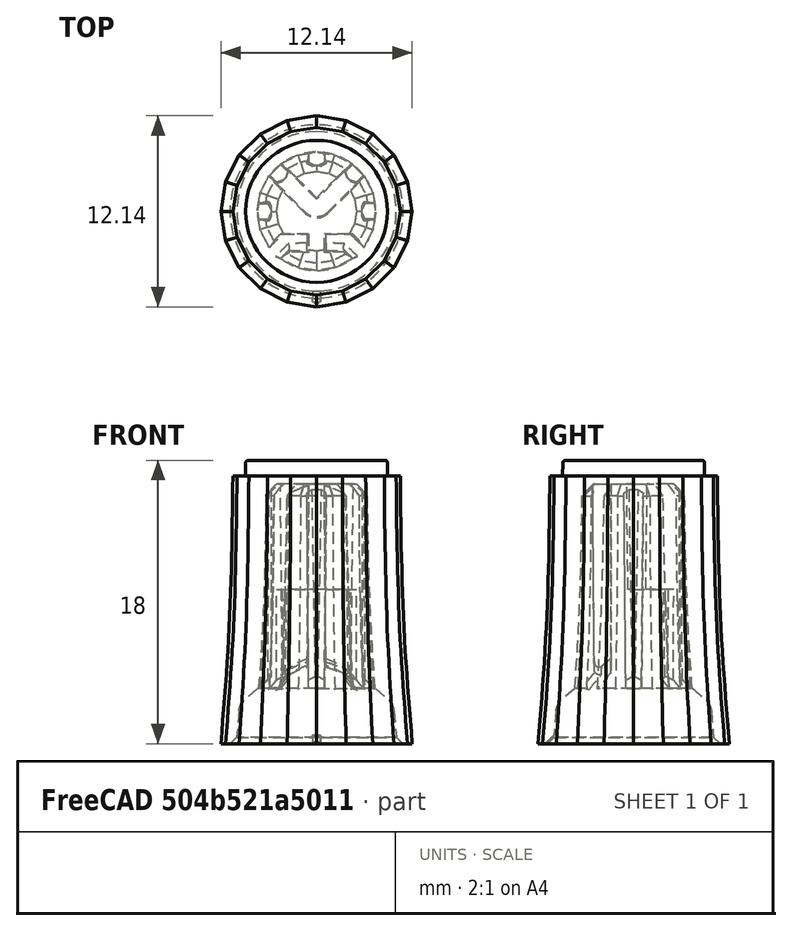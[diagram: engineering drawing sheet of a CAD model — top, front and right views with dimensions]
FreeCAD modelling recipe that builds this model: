
FCSTD DOCUMENT  (FreeCAD 0.21R33668 +26 (Git))
Label: PLASTIC-KNOB-ENC
License: All rights reserved
LicenseURL: https://en.wikipedia.org/wiki/All_rights_reserved
objects: TechDraw::DrawViewDimension×9, TechDraw::DrawHatch×8, TechDraw::DrawViewPart×5, Part::Feature×1, PartDesign::Boolean×1, TechDraw::DrawSVGTemplate×1, Sketcher::SketchObject×1, PartDesign::Body×1, TechDraw::DrawComplexSection×1, TechDraw::DrawViewBalloon×1, TechDraw::DrawPage×1
note: 21 computed .brp shape members not serialized (recipe doc carries the construction recipe); baked Part::Feature solids carry a one-line shape summary decoded from their .brp

FEATURE [Part::Feature] Part__Feature  label="potmeter"
  shape: bbox 15.71 x 15.32 x 34.99 mm, 134 faces (baked)
FEATURE [PartDesign::Boolean] Boolean
  Group = -> [Part__Feature]
  Type = 0
FEATURE [TechDraw::DrawSVGTemplate] Template
  EditableTexts = COLOR=Black - RAL code: 9004; CreationDate=2024/01/02; E.G.APPROVED=APPROVED; FC-Scale=5:1; FC-Title=PLASTIC - KNOB - ENC; IntechStudioLtd.=Intech Studio Ltd.; MATERIAL=ABS - Terluran GP22; REV=02; STANDARD=DIN 16742-TG4
  Height = 297
  Orientation = 1
  Template = <userpath>/Documents/grid-hardware/Manufacturing/FreeCAD_technical_drawing_template/A3_LandscapeTD_MODIFIED.svg
  Width = 420
FEATURE [Sketcher::SketchObject] Sketch
  FullyConstrained = true
  MapMode = 5
  Placement = pos=(0,0,0) rot=(1,0,0;1.5708rad)
  Support = -> [XZ_Plane]
  sketch-geometry (1):
    g0: LineSegment StartX=0 StartY=19 StartZ=0 EndX=0 EndY=-1 EndZ=0
  constraints (4):
    c: PointOnObject(g0,g-2)
    c: Vertical(g0)
    c: DistanceY(g0,g0) = 20
    c: DistanceY(g0,g-1) = 1
FEATURE [PartDesign::Body] Body  label="PLASTIC-KNOB-ENC"
  Group = -> [Boolean,Sketch]
  Origin = -> Origin
  Tip = -> Boolean
FEATURE [TechDraw::DrawViewPart] View
  CoarseView = false
  Direction = (0,-1,0)
  Focus = 100
  HardHidden = false
  IsoCount = 0
  IsoHidden = false
  IsoVisible = true
  LockPosition = false
  Perspective = false
  Rotation = 0
  Scale = 5
  ScaleType = 2
  ScrubCount = 0
  SeamHidden = false
  SeamVisible = true
  SmoothHidden = false
  SmoothVisible = true
  Source = -> [Body]
  X = 98.421
  XDirection = (1,0,-1e-06)
  Y = 192.804
FEATURE [TechDraw::DrawViewPart] View001
  CoarseView = false
  Direction = (-1e-06,0,-1)
  Focus = 100
  HardHidden = false
  IsoCount = 0
  IsoHidden = false
  IsoVisible = true
  LockPosition = false
  Perspective = false
  Rotation = 0
  Scale = 5
  ScaleType = 2
  ScrubCount = 0
  SeamHidden = false
  SeamVisible = true
  SmoothHidden = false
  SmoothVisible = true
  Source = -> [Body]
  X = 305.681
  XDirection = (1,0,-1e-06)
  Y = 190.563
FEATURE [TechDraw::DrawViewPart] View002
  CoarseView = false
  Direction = (1e-06,0,1)
  Focus = 100
  HardHidden = false
  IsoCount = 0
  IsoHidden = false
  IsoVisible = true
  LockPosition = false
  Perspective = false
  Rotation = 0
  Scale = 5
  ScaleType = 2
  ScrubCount = 0
  SeamHidden = false
  SeamVisible = true
  SmoothHidden = false
  SmoothVisible = true
  Source = -> [Body]
  X = 100.462
  XDirection = (1,0,-1e-06)
  Y = 74.8021
FEATURE [TechDraw::DrawComplexSection] ComplexSection  label="Section A - A"
  BaseView = -> View
  Caption = Section A-A
  CoarseView = false
  CutSurfaceDisplay = 2
  CuttingToolWireObject = -> Sketch
  Direction = (-1,0,1e-06)
  FileGeomPattern = C:/Program Files/FreeCAD 0.21/data/Mod/TechDraw/PAT/FCPAT.pat
  FileHatchPattern = C:/Program Files/FreeCAD 0.21/data/Mod/TechDraw/Patterns/simple.svg
  Focus = 100
  FuseBeforeCut = false
  HardHidden = false
  HatchOffset = (0,0,0)
  HatchRotation = 0
  HatchScale = 1
  IsoCount = 0
  IsoHidden = false
  IsoVisible = false
  LockPosition = false
  NameGeomPattern = Gyémánt bevonatú
  Perspective = false
  ProjectionStrategy = 0
  Rotation = -90
  Scale = 5
  ScaleType = 2
  ScrubCount = 0
  SeamHidden = false
  SeamVisible = true
  SectionDirection = 4
  SectionNormal = (-1,0,1e-06)
  SectionOrigin = (0,0,0)
  SectionSymbol = A
  SmoothHidden = false
  SmoothVisible = true
  Source = -> [Body]
  TrimAfterCut = false
  X = 193.37
  XDirection = (-1e-06,0,-1)
  Y = 193.697
FEATURE [TechDraw::DrawHatch] Hatch  label="HatchF1"
  HatchPattern = C:/Program Files/FreeCAD 0.21/data/Mod/TechDraw/Patterns/simple.svg
  Source = -> ComplexSection [Face1]
FEATURE [TechDraw::DrawViewDimension] Dimension
  AngleOverride = false
  Arbitrary = false
  ArbitraryTolerances = false
  EqualTolerance = true
  ExtensionAngle = 0
  FormatSpec = %.2w
  FormatSpecOverTolerance = %+.2w
  FormatSpecUnderTolerance = %+.2w
  Inverted = false
  LineAngle = 0
  LockPosition = false
  MeasureType = 1
  OverTolerance = 0.1
  References2D = -> [ComplexSection]
  Rotation = 0
  ScaleType = 0
  TheoreticalExact = false
  Type = 2
  UnderTolerance = -0.1
  X = 46.2416
  Y = -17.976
FEATURE [TechDraw::DrawViewDimension] Dimension001
  AngleOverride = false
  Arbitrary = false
  ArbitraryTolerances = false
  EqualTolerance = false
  ExtensionAngle = 0
  FormatSpec = ⌀%.1w
  FormatSpecOverTolerance = %+.2w
  FormatSpecUnderTolerance = %+.2w
  Inverted = false
  LineAngle = 0
  LockPosition = false
  MeasureType = 1
  OverTolerance = 0.1
  References2D = -> [ComplexSection]
  Rotation = 0
  ScaleType = 0
  TheoreticalExact = false
  Type = 1
  UnderTolerance = 0
  X = 45.3884
  Y = -50.1957
FEATURE [TechDraw::DrawViewDimension] Dimension003
  AngleOverride = false
  Arbitrary = false
  ArbitraryTolerances = false
  EqualTolerance = true
  ExtensionAngle = 0
  FormatSpec = %.2w
  FormatSpecOverTolerance = %+.2w
  FormatSpecUnderTolerance = %+.2w
  Inverted = false
  LineAngle = 0
  LockPosition = false
  MeasureType = 1
  OverTolerance = 0
  References2D = -> [View]
  Rotation = 0
  ScaleType = 0
  TheoreticalExact = false
  Type = 2
  UnderTolerance = 0
  X = -57.7221
  Y = 0.521046
FEATURE [TechDraw::DrawViewDimension] Dimension004
  AngleOverride = false
  Arbitrary = false
  ArbitraryTolerances = false
  EqualTolerance = true
  ExtensionAngle = 0
  FormatSpec = %.2w
  FormatSpecOverTolerance = %+.2w
  FormatSpecUnderTolerance = %+.2w
  Inverted = false
  LineAngle = 0
  LockPosition = false
  MeasureType = 1
  OverTolerance = 0
  References2D = -> [View]
  Rotation = 0
  ScaleType = 0
  TheoreticalExact = false
  Type = 2
  UnderTolerance = 0
  X = 39.126
  Y = 37.6793
FEATURE [TechDraw::DrawViewDimension] Dimension005
  AngleOverride = false
  Arbitrary = false
  ArbitraryTolerances = false
  EqualTolerance = true
  ExtensionAngle = 0
  FormatSpec = ⌀%.2w
  FormatSpecOverTolerance = %+.2w
  FormatSpecUnderTolerance = %+.2w
  Inverted = false
  LineAngle = 0
  LockPosition = false
  MeasureType = 1
  OverTolerance = 0
  References2D = -> [View001]
  Rotation = 0
  ScaleType = 0
  TheoreticalExact = false
  Type = 5
  UnderTolerance = 0
  X = -41.2084
  Y = 24.1058
FEATURE [TechDraw::DrawViewDimension] Dimension006
  AngleOverride = false
  Arbitrary = true
  ArbitraryTolerances = false
  EqualTolerance = true
  ExtensionAngle = 0
  FormatSpec = 5,797±0,05
  FormatSpecOverTolerance = %+.2w
  FormatSpecUnderTolerance = %+.2w
  Inverted = false
  LineAngle = 0
  LockPosition = false
  MeasureType = 1
  OverTolerance = 0.05
  References2D = -> [View001]
  Rotation = 0
  ScaleType = 0
  TheoreticalExact = false
  Type = 1
  UnderTolerance = -0.05
  X = -0.153255
  Y = 40.8913
FEATURE [TechDraw::DrawViewDimension] Dimension007
  AngleOverride = false
  Arbitrary = false
  ArbitraryTolerances = false
  EqualTolerance = true
  ExtensionAngle = 0
  FormatSpec = %.2w
  FormatSpecOverTolerance = %+.2w
  FormatSpecUnderTolerance = %+.2w
  Inverted = false
  LineAngle = 0
  LockPosition = false
  MeasureType = 1
  OverTolerance = 0.05
  References2D = -> [View001]
  Rotation = 0
  ScaleType = 0
  TheoreticalExact = false
  Type = 2
  UnderTolerance = -0.05
  X = 40.9222
  Y = 25.266
FEATURE [TechDraw::DrawViewDimension] Dimension008
  AngleOverride = false
  Arbitrary = false
  ArbitraryTolerances = false
  EqualTolerance = true
  ExtensionAngle = 0
  FormatSpec = ⌀%.0w
  FormatSpecOverTolerance = %+.2w
  FormatSpecUnderTolerance = %+.2w
  Inverted = false
  LineAngle = 0
  LockPosition = false
  MeasureType = 1
  OverTolerance = 0
  References2D = -> [View]
  Rotation = 0
  ScaleType = 0
  TheoreticalExact = false
  Type = 1
  UnderTolerance = 0
  X = -8.5e-05
  Y = 63.706
FEATURE [TechDraw::DrawViewDimension] Dimension009
  AngleOverride = false
  Arbitrary = false
  ArbitraryTolerances = false
  EqualTolerance = true
  ExtensionAngle = 0
  FormatSpec = 10× %.2w
  FormatSpecOverTolerance = %+.2w
  FormatSpecUnderTolerance = %+.2w
  Inverted = false
  LineAngle = 0
  LockPosition = false
  MeasureType = 1
  OverTolerance = 0
  References2D = -> [View002]
  Rotation = 0
  ScaleType = 0
  TheoreticalExact = false
  Type = 0
  UnderTolerance = 0
  X = -39.2324
  Y = 9.93901
FEATURE [TechDraw::DrawViewPart] View003
  CoarseView = false
  Direction = (-0.57735,-0.57735,0.57735)
  Focus = 100
  HardHidden = false
  IsoCount = 0
  IsoHidden = false
  IsoVisible = true
  LockPosition = false
  Perspective = false
  Rotation = 0
  Scale = 2
  ScaleType = 2
  ScrubCount = 0
  SeamHidden = false
  SeamVisible = true
  SmoothHidden = false
  SmoothVisible = true
  Source = -> [Body]
  X = 364.887
  XDirection = (0.707107,-0.707107,0)
  Y = 107.169
FEATURE [TechDraw::DrawViewPart] View004
  CoarseView = false
  Direction = (-0.57735,-0.57735,-0.57735)
  Focus = 100
  HardHidden = false
  IsoCount = 0
  IsoHidden = false
  IsoVisible = true
  LockPosition = false
  Perspective = false
  Rotation = 0
  Scale = 2
  ScaleType = 2
  ScrubCount = 0
  SeamHidden = false
  SeamVisible = true
  SmoothHidden = false
  SmoothVisible = true
  Source = -> [Body]
  X = 323.57
  XDirection = (0.707106,-0.707106,0)
  Y = 108.033
FEATURE [TechDraw::DrawHatch] Hatch001  label="Hatch001F2"
  HatchPattern = C:/Program Files/FreeCAD 0.21/data/Mod/TechDraw/Patterns/solid.svg
  Source = -> View003 [Face2,Face13,Face4,Face5,Face3,Face6,Face9,Face8,Face7,Face12,Face11,Face10]
FEATURE [TechDraw::DrawHatch] Hatch002  label="Hatch002F1"
  HatchPattern = C:/Program Files/FreeCAD 0.21/data/Mod/TechDraw/Patterns/solid.svg
  Source = -> View003 [Face1]
FEATURE [TechDraw::DrawHatch] Hatch003  label="Hatch003F19"
  HatchPattern = C:/Program Files/FreeCAD 0.21/data/Mod/TechDraw/Patterns/solid.svg
  Source = -> View004 [Face19,Face8,Face4,Face7,Face3,Face5,Face6,Face9,Face13,Face14]
FEATURE [TechDraw::DrawHatch] Hatch004  label="Hatch004F16"
  HatchPattern = C:/Program Files/FreeCAD 0.21/data/Mod/TechDraw/Patterns/solid.svg
  Source = -> View004 [Face16,Face22,Face23,Face11,Face18,Face21]
FEATURE [TechDraw::DrawHatch] Hatch005  label="Hatch005F15"
  HatchPattern = C:/Program Files/FreeCAD 0.21/data/Mod/TechDraw/Patterns/solid.svg
  Source = -> View004 [Face15,Face20,Face17,Face10,Face1,Face12]
FEATURE [TechDraw::DrawHatch] Hatch006  label="Hatch006F32"
  HatchPattern = C:/Program Files/FreeCAD 0.21/data/Mod/TechDraw/Patterns/solid.svg
  Source = -> View004 [Face32,Face31,Face24,Face25,Face27,Face28,Face29,Face30,Face33]
FEATURE [TechDraw::DrawHatch] Hatch007  label="Hatch007F34"
  HatchPattern = C:/Program Files/FreeCAD 0.21/data/Mod/TechDraw/Patterns/solid.svg
  Source = -> View004 [Face34]
FEATURE [TechDraw::DrawViewBalloon] Balloon
  BubbleShape = 1
  EndType = 3
  EndTypeScale = 1
  KinkLength = -0.1
  LockPosition = false
  OriginX = -1.85535
  OriginY = 3.61508
  Rotation = 0
  ScaleType = 0
  ShapeScale = 1
  SourceView = -> View004
  Text = AESTHETICAL SURFACES:\nCOLORED BLUE ON THE DRAWING: SPI - D1\nNO BURRS, NO PARTING LINES,\nNO EJECTION MARKS\nFREE OF ANY DEFECTS\nNON VISIBLE GATE LOCATION ALLOWED\nREMAINING BLACK SURFACES: SPI - B2
  TextWrapLen = -1
  X = -33.0088
  Y = -3.78312
FEATURE [TechDraw::DrawPage] Page  label="PLASTIC-KNOB-ENC_Drawing"
  KeepUpdated = true
  NextBalloonIndex = 2
  ProjectionType = 0
  Template = -> Template
  Views = -> [View,View001,View002,ComplexSection,Dimension,Dimension001,Dimension003,Dimension004,Dimension005,Dimension006,Dimension007,Dimension008,Dimension009,View003,View004,Balloon]
